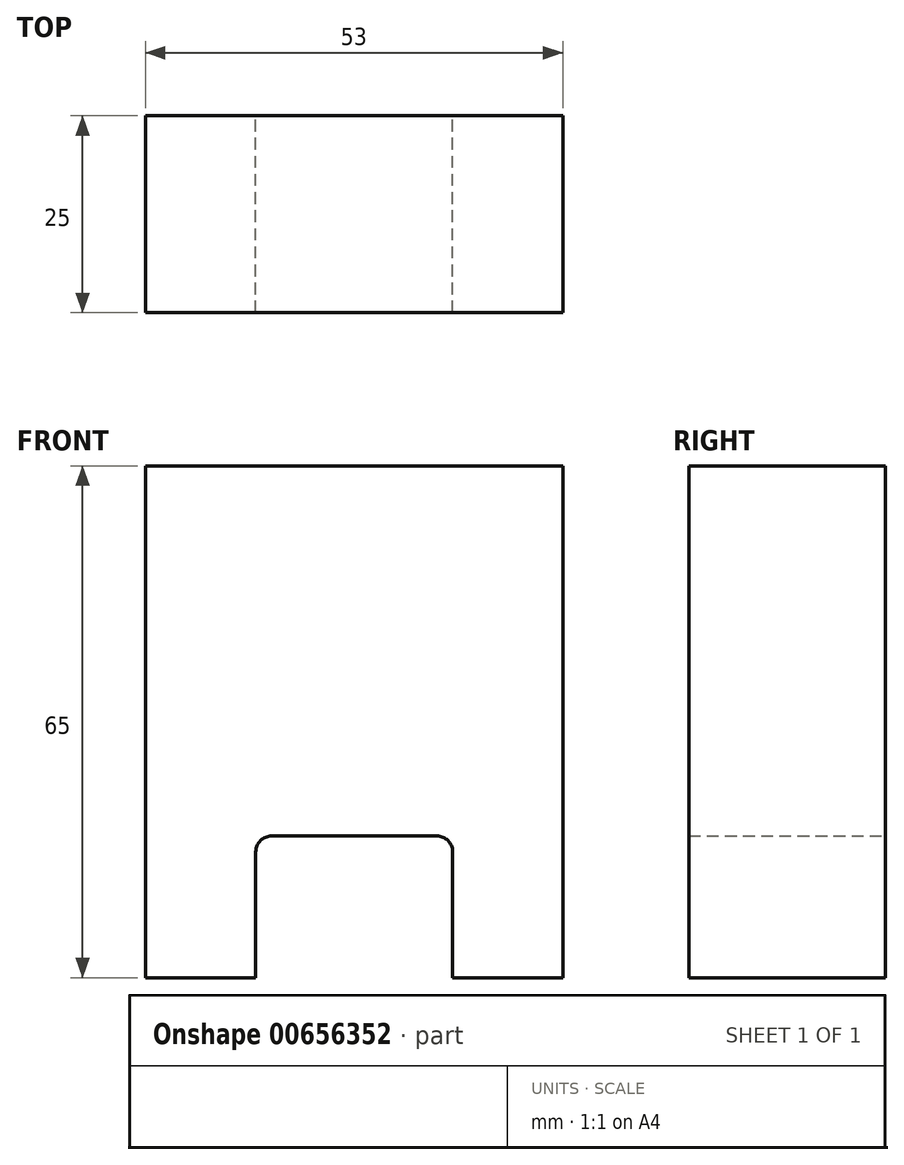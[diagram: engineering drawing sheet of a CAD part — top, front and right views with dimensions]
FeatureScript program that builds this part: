
annotation { "Feature Type Name" : "Feature", "Feature Type Description" : "" }
export const myFeature = defineFeature(function(context is Context, id is Id, definition is map)
    precondition{}
    {
        {
            var Q0;
            Q0=qCreatedBy(makeId("Front.planeOp"),FACE);
            var sketch = newSketch(context, id + "F0", { "sketchPlane" : qUnion([Q0])});
            skLineSegment(sketch, "E0", {"start": v(0, 0) * mm, "end": v(14, 0) * mm});
            skLineSegment(sketch, "E1", {"start": v(14, 0) * mm, "end": v(14, 65) * mm});
            skLineSegment(sketch, "E2", {"start": v(14, 65) * mm, "end": v(-39, 65) * mm});
            skLineSegment(sketch, "E3", {"start": v(-39, 65) * mm, "end": v(-39, 0) * mm});
            skLineSegment(sketch, "E4", {"start": v(-39, 0) * mm, "end": v(-25, 0) * mm});
            skLineSegment(sketch, "E5", {"start": v(-25, 0) * mm, "end": v(-25, 16) * mm});
            skLineSegment(sketch, "E6", {"start": v(-23, 18) * mm, "end": v(-2, 18) * mm});
            skLineSegment(sketch, "E7", {"start": v(0, 16) * mm, "end": v(0, 0) * mm});
            skPoint(sketch, "E8.visualSharp", {"position": v(-25, 18) * mm});
            skArc(sketch, "E8.filletArc", {"start": v(-23, 18) * mm, "mid": v(-24.41, 17.41) * mm, "end": v(-25, 16) * mm});
            skPoint(sketch, "E9.visualSharp", {"position": v(0, 18) * mm});
            skArc(sketch, "E9.filletArc", {"start": v(0, 16) * mm, "mid": v(-0.59, 17.41) * mm, "end": v(-2, 18) * mm});
            skSolve(sketch);
        }
        {
            var Q0;
            Q0=makeQuery(id+"F0.imprint","IMPRINT",FACE,{"disambiguationData":[TD([[makeQuery(id+"F0.imprint","IMPRINT",EDGE,{"derivedFrom":sQuery(id+"F0.wireOp",EDGE,"E0")}),1.0]])]});
            extrude(context, id + "F1", {"entities" : qUnion([Q0]), "depth" : 25 * mm, "offsetDistance" : 25 * mm});
        }
    });
